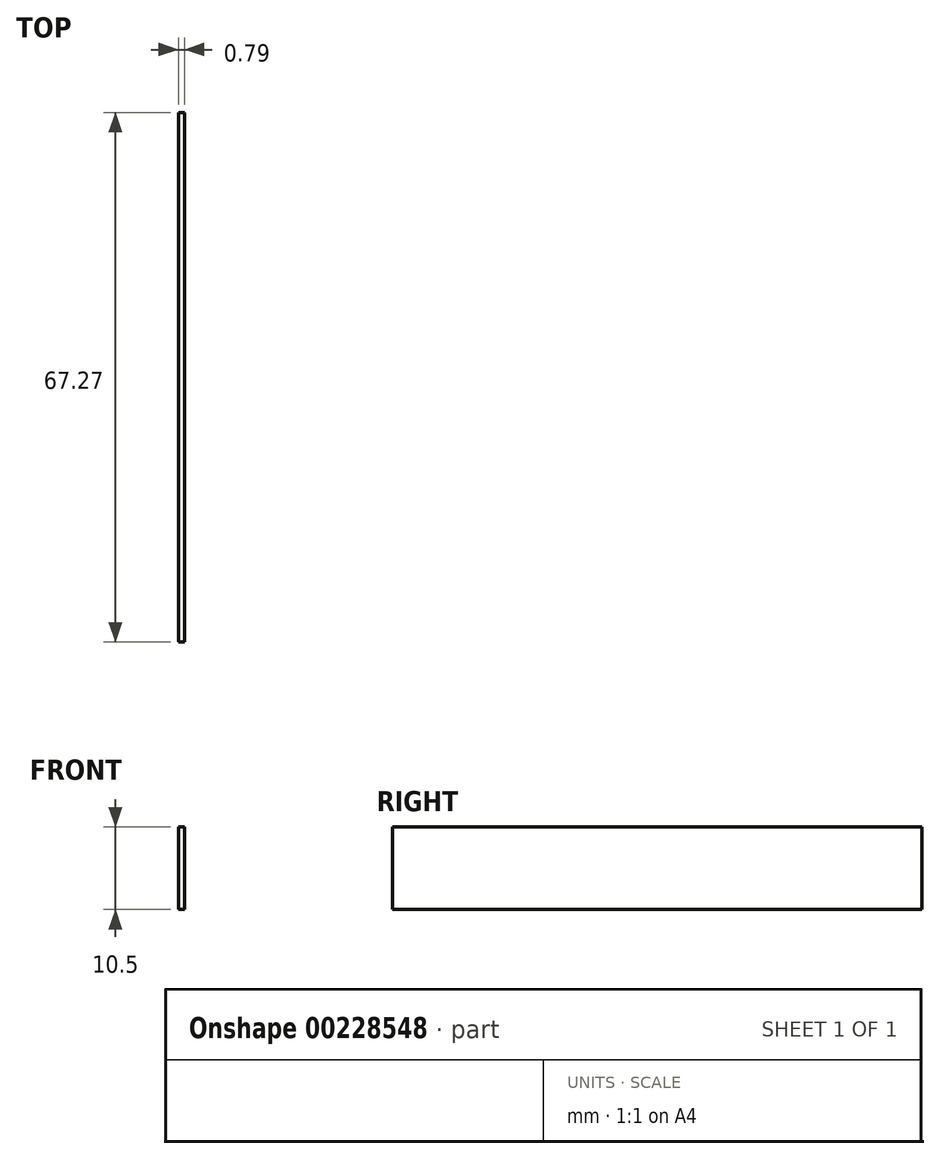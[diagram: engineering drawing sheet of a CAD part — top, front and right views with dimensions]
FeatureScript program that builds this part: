
annotation { "Feature Type Name" : "Feature", "Feature Type Description" : "" }
export const myFeature = defineFeature(function(context is Context, id is Id, definition is map)
    precondition{}
    {
        {
            var Q0;
            Q0=qCreatedBy(makeId("Right.planeOp"),FACE);
            var sketch = newSketch(context, id + "F0", { "sketchPlane" : qUnion([Q0])});
            skLineSegment(sketch, "E0.bottom", {"start": v(0, 0) * mm, "end": v(5859.3, 0) * mm});
            skLineSegment(sketch, "E0.top", {"start": v(0, 914.4) * mm, "end": v(5859.3, 914.4) * mm});
            skLineSegment(sketch, "E0.left", {"start": v(0, 0) * mm, "end": v(0, 914.4) * mm});
            skLineSegment(sketch, "E0.right", {"start": v(5859.3, 0) * mm, "end": v(5859.3, 914.4) * mm});
            skSolve(sketch);
        }
        {
            var Q0;
            Q0=makeQuery(id+"F0.imprint","IMPRINT",FACE,{"disambiguationData":[TD([[makeQuery(id+"F0.imprint","IMPRINT",EDGE,{"derivedFrom":sQuery(id+"F0.wireOp",EDGE,"E0.bottom")}),1.0]])]});
            extrude(context, id + "F1", {"entities" : qUnion([Q0]), "depth" : 69.14 * mm});
        }
        {
            var Q0;
            Q0=makeQuery(id+"F1.opExtrude","SWEPT_BODY",BODY,{"disambiguationData":[OSD([sQuery(id+"F0.wireOp",EDGE,"E0.bottom"),sQuery(id+"F0.wireOp",EDGE,"E0.top"),sQuery(id+"F0.wireOp",EDGE,"E0.left"),sQuery(id+"F0.wireOp",EDGE,"E0.right")])]});
            var Q1;
            Q1=qCreatedBy(makeId("Origin.pointOp"),VERTEX);
            transform(context, id + "F2", {"entities" : qUnion([Q0]), "transformType" : TransformType.SCALE_UNIFORMLY, "scale" : 1 / 87.1, "scalePoint" : qUnion([Q1]), "makeCopy" : false});
        }
    });
